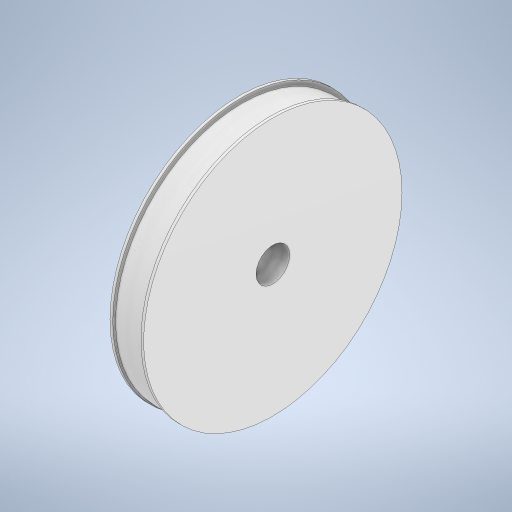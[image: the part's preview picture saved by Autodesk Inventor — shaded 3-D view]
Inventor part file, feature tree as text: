
AUTODESK INVENTOR PART (.ipt)
format: ipt  version: 2023 (Build 270158000, 158)  size: 252,928 bytes
history: native  units: mm
features: sketch x5, extrude x4, other x1
ambient origin geometry x8: Origin, YZ Plane, XZ Plane, XY Plane, X Axis, Y Axis, Z Axis, Center Point
bodies: Body1 (feature_tree)
feature tree (10):
  other  "ソリッド1"
  extrude  "押し出し1"  Depth=90.0mm
  extrude  "押し出し2"  Depth=10.0mm TaperAngle=0.0deg
  extrude  "押し出し3"  Depth=92.0mm
  sketch  "スケッチ4"
  extrude  "押し出し4"  Depth=1.0mm TaperAngle=0.0deg
  sketch  "スケッチ1"
  sketch  "スケッチ2"
  sketch  "スケッチ3"
  sketch  "スケッチ5"
